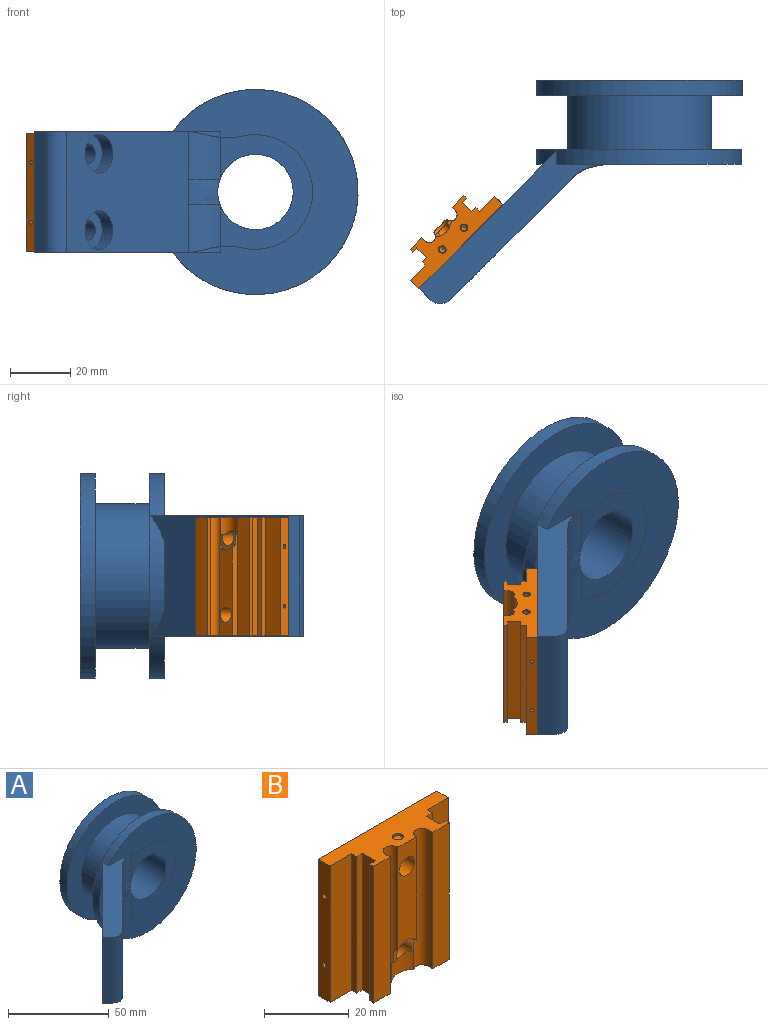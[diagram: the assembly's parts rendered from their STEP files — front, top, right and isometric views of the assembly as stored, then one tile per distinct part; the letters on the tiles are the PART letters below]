
ASSEMBLY  parts=2 mates=1
PART A: 30 faces, bbox 107.7x74.6x68.6 mm
  f0: cylinder r=3.25mm len=8.13mm, axis (0.71,-0.71,0), area 102.1mm2, adj f13,f28
  f1: cylinder r=3.25mm len=8.13mm, axis (0.71,-0.71,0), area 102.1mm2, adj f13,f26
  f2: plane 23.53x2.1mm, normal (0,-1,0), area 33.1mm2, adj f7,f13
  f3: plane 68x61.5mm, normal (0,-1,0), area 1825.2mm2, adj f4,f7,f16,f17,f18,f19,f20,f22
  f4: cylinder r=19mm len=38mm, axis (0,1,0), area 13.7mm2, adj f3,f5,f19,f22
  f5: plane 38x30.74mm, normal (0,-1,0), area 511.7mm2, adj f4,f12,f19,f21,f22,f24
  f6: cylinder r=24mm len=48mm, axis (0,1,0), area 2684.2mm2, adj f8,f11
  f7: cylinder r=34mm len=68mm, axis (0,1,0), area 1026.9mm2, adj f2,f3,f8,f13,f16,f17
  f8: plane 68x68mm, normal (0,1,0), area 1822.1mm2, adj f6,f7
  f9: cylinder r=34mm len=68mm, axis (0,-1,0), area 1068.1mm2, adj f10,f11
  f10: plane 68x68mm, normal (0,1,0), area 3140.8mm2, adj f9,f12
  f11: plane 68x68mm, normal (0,-1,0), area 1822.1mm2, adj f6,f9
  f12: cylinder r=12.5mm len=28mm, axis (0,1,0), area 2199.1mm2, adj f5,f10,f23
  f13: plane 46.17x46.17mm, normal (-0.71,0.71,0), area 2309.9mm2, adj f0,f1,f2,f7,f14,f16,f17
  f14: plane 40x3.54mm, normal (-0.71,-0.71,0), area 200mm2, adj f13,f16,f17,f29
  f15: plane 40.16x40.16mm, normal (0.71,-0.71,0), area 2005.4mm2, adj f16,f17,f21,f23,f24,f25,f27,f29
  f16: plane 61.56x50.6mm, normal (0,0,1), area 641.8mm2, adj f3,f7,f13,f14,f15,f20,f22,f29
  f17: plane 61.56x50.6mm, normal (0,0,-1), area 641.8mm2, adj f3,f7,f13,f14,f15,f18,f19,f29
  f18: cylinder r=15mm len=10.61mm, axis (0,0,1), area 11.1mm2, adj f3,f17,f19
  f19: bspline ~21.5x20.9mm, area 2.9mm2, adj f3,f4,f5,f17,f18,f21
  f20: cylinder r=15mm len=10.61mm, axis (0,0,1), area 11.1mm2, adj f3,f16,f22
  f21: cylinder r=15mm len=15.72mm, axis (0,0,1), area 173.9mm2, adj f5,f15,f19,f23
  f22: bspline ~21.5x20.9mm, area 2.9mm2, adj f3,f4,f5,f16,f20,f24
  f23: bspline ~12.77x11.68mm, area 96.4mm2, adj f12,f15,f21,f24
  f24: cylinder r=15mm len=15.72mm, axis (0,0,1), area 173.9mm2, adj f5,f15,f22,f23
  f25: cylinder r=6.5mm len=13mm, axis (0.71,-0.71,0), area 204.2mm2, adj f15,f26
  f26: plane 13x9.19mm, normal (0.71,-0.71,0), area 99.5mm2, adj f1,f25
  f27: cylinder r=6.5mm len=13mm, axis (0.71,-0.71,0), area 204.2mm2, adj f15,f28
  f28: plane 13x9.19mm, normal (0.71,-0.71,0), area 99.5mm2, adj f0,f27
  f29: cylinder r=5mm len=40mm, axis (0,0,-1), area 314.2mm2, adj f14,f15,f16,f17
PART B: 69 faces, bbox 39.4x11.3x39.4 mm
  f0: cone r=1mm half-angle=59deg, axis (0,0,-1), area 3.6mm2, adj f4
  f1: cone r=1mm half-angle=59deg, axis (0,0,-1), area 3.6mm2, adj f5
  f2: plane 1.19x1.19mm, normal (1,0,0), area 1.1mm2, adj f10
  f3: plane 1.19x1.19mm, normal (1,0,0), area 1.1mm2, adj f11
  f4: cylinder r=1mm len=5.59mm, axis (0,0,-1), area 35mm2, adj f0,f12
  f5: cylinder r=1mm len=5.59mm, axis (0,0,-1), area 35mm2, adj f1,f13
  f6: plane 1.19x1.19mm, normal (-1,0,0), area 1.1mm2, adj f14
  f7: plane 1.19x1.19mm, normal (-1,0,0), area 1.1mm2, adj f15
  f8: plane 2.64x2.64mm, normal (0,0,1), area 5.5mm2, adj f35
  f9: cylinder r=3.61mm len=6.7mm, axis (0,-1,0), area 8.2mm2, adj f24,f25,f26,f48
  f10: cylinder r=0.6mm len=3.81mm, axis (1,0,0), area 14.3mm2, adj f2,f51
  f11: cylinder r=0.6mm len=3.81mm, axis (1,0,0), area 14.3mm2, adj f3,f51
  f12: cone r=1.25mm half-angle=45deg, axis (0,0,-1), area 2.5mm2, adj f4,f52
  f13: cone r=1.25mm half-angle=45deg, axis (0,0,-1), area 2.5mm2, adj f5,f52
  f14: cylinder r=0.6mm len=3.81mm, axis (-1,0,0), area 14.3mm2, adj f6,f53
  f15: cylinder r=0.6mm len=3.81mm, axis (-1,0,0), area 14.3mm2, adj f7,f53
  f16: plane 39.37x7.06mm, normal (0,-1,0), area 278mm2, adj f17,f52,f53,f54
  f17: plane 39.37x1.78mm, normal (-1,0,0), area 70mm2, adj f16,f18,f52,f54
  f18: plane 39.37x1.96mm, normal (0,-1,0), area 77mm2, adj f17,f19,f52,f54
  f19: plane 39.37x4.39mm, normal (-1,0,0), area 173mm2, adj f18,f20,f52,f54
  f20: plane 39.37x1.96mm, normal (0,1,0), area 77mm2, adj f19,f21,f52,f54
  f21: plane 39.37x1.27mm, normal (-1,0,0), area 50mm2, adj f20,f22,f52,f54
  f22: plane 39.37x5.51mm, normal (0,-1,0), area 217mm2, adj f21,f23,f52,f54
  f23: plane 39.37x1.47mm, normal (1,0,0), area 58mm2, adj f22,f24,f52,f54
  f24: cylinder r=2.03mm len=39.37mm, axis (0,0,1), area 237.1mm2, adj f9,f23,f25,f46,f47,f48,f52,f54
  f25: plane 29.82x6.1mm, normal (0,-1,0), area 154.1mm2, adj f9,f24,f26,f54,f56
  f26: cylinder r=2.03mm len=39.37mm, axis (0,0,1), area 237.1mm2, adj f9,f25,f27,f45,f46,f48,f52,f54
  f27: plane 39.37x1.47mm, normal (-1,0,0), area 58mm2, adj f26,f28,f52,f54
  f28: plane 39.37x5.51mm, normal (0,-1,0), area 217mm2, adj f27,f29,f52,f54
  f29: plane 39.37x1.27mm, normal (1,0,0), area 50mm2, adj f28,f30,f52,f54
  f30: plane 39.37x1.96mm, normal (0,1,0), area 77mm2, adj f29,f31,f52,f54
  f31: plane 39.37x4.39mm, normal (1,0,0), area 173mm2, adj f30,f32,f52,f54
  f32: plane 39.37x1.96mm, normal (0,-1,0), area 77mm2, adj f31,f33,f52,f54
  f33: plane 39.37x1.78mm, normal (1,0,0), area 70mm2, adj f32,f34,f52,f54
  f34: plane 39.37x7.06mm, normal (0,-1,0), area 278mm2, adj f33,f51,f52,f54
  f35: cylinder r=1.32mm len=2.64mm, axis (0,0,-1), area 5.3mm2, adj f8,f54
  f36: plane 5.11x5.11mm, normal (0,1,0), area 20.5mm2, adj f55
  f37: plane 3.45x3.45mm, normal (0,1,0), area 9.4mm2, adj f57
  f38: plane 3.45x3.45mm, normal (0,1,0), area 9.4mm2, adj f58
  f39: plane 3.45x3.45mm, normal (0,1,0), area 9.4mm2, adj f59
  f40: plane 3.45x3.45mm, normal (0,1,0), area 9.4mm2, adj f60
  f41: plane 3.45x3.45mm, normal (0,1,0), area 9.4mm2, adj f61
  f42: plane 3.45x3.45mm, normal (0,1,0), area 9.4mm2, adj f62
  f43: plane 3.45x3.45mm, normal (0,1,0), area 9.4mm2, adj f63
  f44: plane 3.45x3.45mm, normal (0,1,0), area 9.4mm2, adj f64
  f45: plane 1.48x1.44mm, normal (0,0,-1), area 1.4mm2, adj f26,f46,f48,f65
  f46: cylinder r=5.59mm len=7.52mm, axis (0,0,-1), area 43.5mm2, adj f24,f26,f45,f47,f52,f65
  f47: plane 1.48x1.44mm, normal (0,0,-1), area 1.4mm2, adj f24,f46,f48,f65
  f48: plane 6.7x5.39mm, normal (0,-1,0), area 16mm2, adj f9,f24,f26,f45,f47,f65
  f49: plane 2.26x2.26mm, normal (0,1,0), area 4mm2, adj f66
  f50: plane 2.26x2.26mm, normal (0,1,0), area 4mm2, adj f67
  f51: plane 39.37x3.81mm, normal (1,0,0), area 147.8mm2, adj f10,f11,f34,f52,f54,f68
  f52: plane 39.37x11.25mm, normal (0,0,-1), area 259.4mm2, adj f12,f13,f16,f17,f18,f19,f20,f21
  f53: plane 39.37x3.81mm, normal (-1,0,0), area 147.8mm2, adj f14,f15,f16,f52,f54,f68
  f54: plane 39.37x11.25mm, normal (0,0,1), area 281.3mm2, adj f16,f17,f18,f19,f20,f21,f22,f23
  f55: cylinder r=2.55mm len=6.35mm, axis (0,1,0), area 101.8mm2, adj f36,f68
  f56: cylinder r=2.55mm len=9.78mm, axis (0,1,0), area 156.8mm2, adj f25,f68
  f57: cylinder r=1.73mm len=6.35mm, axis (0,1,0), area 68.9mm2, adj f37,f68
  f58: cylinder r=1.73mm len=6.35mm, axis (0,1,0), area 68.9mm2, adj f38,f68
  f59: cylinder r=1.73mm len=6.35mm, axis (0,1,0), area 68.9mm2, adj f39,f68
  f60: cylinder r=1.73mm len=6.35mm, axis (0,1,0), area 68.9mm2, adj f40,f68
  f61: cylinder r=1.73mm len=6.35mm, axis (0,1,0), area 68.9mm2, adj f41,f68
  f62: cylinder r=1.73mm len=6.35mm, axis (0,1,0), area 68.9mm2, adj f42,f68
  f63: cylinder r=1.73mm len=6.35mm, axis (0,1,0), area 68.9mm2, adj f43,f68
  f64: cylinder r=1.73mm len=6.35mm, axis (0,1,0), area 68.9mm2, adj f44,f68
  f65: cylinder r=2.55mm len=8.71mm, axis (0,1,0), area 129.9mm2, adj f45,f46,f47,f48,f68
  f66: cylinder r=1.13mm len=4.32mm, axis (0,1,0), area 30.7mm2, adj f49,f68
  f67: cylinder r=1.13mm len=4.32mm, axis (0,1,0), area 30.7mm2, adj f50,f68
  f68: plane 39.37x39.37mm, normal (0,1,0), area 1405.6mm2, adj f51,f52,f53,f54,f55,f56,f57,f58
PLACE A t=(-41.95,-14.08,-19.33)mm
PLACE B rot(axis=(-0.92,-0.38,0),180deg) t=(-128.32,-64.45,-39.15)mm
MATE planar B.f66 <-> A.f13  axis (0.71,-0.71,0) through (-108.59,-71.61,-3.59)mm
